# Revit family: NLRSen_57_AT_UN_PRxD_Solid_Air
name_source: partatom
category: Air Terminals
revit_build: Autodesk Revit 2017 (Build: 20190508_0315(x64)
units: mm (PartAtom-declared; Revit-internal decimal feet)

## family parameters
Always vertical = Yes
Cut with Voids When Loaded = No
OmniClass Number = 23.75.70.21.27.11
OmniClass Title = Diffusers, Registers, and Grilles
Part Type = Normal
Room Calculation Point = Yes
Round Connector Dimension = Use Diameter
Shared = No
Work Plane-Based = No

## types (5) — shared parameters
Description = Flanged perforated return grill, Type PRVD and PRDD
IfcDescription = Flanged perforated return grill, Type PRVD and PRDD
IfcExportAs = IfcAirterminal
IfcExportType = Diffuser
Lookup_Article_Codes = Grill_Article_Codes
Lookup_Article_Data = PRxD_Article_Data
Lookup_Article_Names = Grill_Article_Names
Lookup_Grill_Factors = Grill_Selection_Factors
Manufacturer = Solid Air Climate Solutions
Model = PRxD
NLRS_C_content_datum_uitgifte = 2019-09-17
NLRS_C_content_provider = Solid Air Climate Solutions
NLRS_C_content_versie = 2.03
NLRS_C_description = Flanged perforated return grill, Type PRVD and PRDD
SACS_AX_Prefix = 800
SACS_Plenum_Material = Sendzimir verzinkt
SACS_Revised_ by = J. Feeke
SACS_Revision_Date = 2019-09-17
SACS_Revision_Number = 2.03
Type Comments = Please make sure flow is set to m3/h!
URL = https://solid-air.nl
zero-valued in all types: Cost

## per-type parameters (varying)
| type | Assembly Code | Max Flow | Min Flow | SACS_Base_Index | SACS_Plenum_A | SACS_Plenum_B | SACS_Plenum_D1 | SACS_Plenum_D2 | SACS_Plenum_D2oval_H | SACS_Plenum_D2oval_W | SACS_Plenum_P | SACS_Plenum_Plow | SACS_Plenum_Poval | SACS_Plenum_T |
| 250 | 57.71 | 216 m³/h | 54 m³/h | 1 | 242 mm  [stored 0.793963 ft] | 249 mm  [stored 0.816929 ft] | 123 mm  [stored 0.403543 ft] | 123 mm  [stored 0.403543 ft] | 73 mm  [stored 0.239501 ft] | 164 mm  [stored 0.538058 ft] | 235 mm  [stored 0.770997 ft] | 220 mm  [stored 0.721785 ft] | 160 mm  [stored 0.524934 ft] | 70 mm  [stored 0.229659 ft] |
| 300 | 57 | 360 m³/h | 90 m³/h | 2 | 307 mm  [stored 1.00722 ft] | 313 mm  [stored 1.0269 ft] | 158 mm | 158 mm | 93 mm  [stored 0.305118 ft] | 208 mm | 270 mm  [stored 0.885827 ft] | 255 mm  [stored 0.836614 ft] | 180 mm  [stored 0.590551 ft] | 70 mm  [stored 0.229659 ft] |
| 400 | 57 | 540 m³/h | 144 m³/h | 3 | 382 mm  [stored 1.25328 ft] | 388 mm  [stored 1.27297 ft] | 198 mm  [stored 0.649606 ft] | 198 mm  [stored 0.649606 ft] | 117 mm  [stored 0.383858 ft] | 262 mm  [stored 0.85958 ft] | 315 mm  [stored 1.03346 ft] | 300 mm  [stored 0.984252 ft] | 210 mm  [stored 0.688976 ft] | 75 mm  [stored 0.246063 ft] |
| 500 | 57 | 720 m³/h | 216 m³/h | 4 | 477 mm  [stored 1.56496 ft] | 483 mm | 248 mm  [stored 0.813648 ft] | 198 mm  [stored 0.649606 ft] | 117 mm  [stored 0.383858 ft] | 262 mm  [stored 0.85958 ft] | 325 mm  [stored 1.06627 ft] | 310 mm  [stored 1.01706 ft] | 220 mm  [stored 0.721785 ft] | 85 mm  [stored 0.278871 ft] |
| 550 | 57 | 1080 m³/h | 288 m³/h | 5 | 551 mm  [stored 1.80774 ft] | 556 mm  [stored 1.82415 ft] | 313 mm  [stored 1.0269 ft] | 248 mm  [stored 0.813648 ft] | 147 mm  [stored 0.482283 ft] | 330 mm  [stored 1.08268 ft] | 395 mm  [stored 1.29593 ft] | 365 mm  [stored 1.19751 ft] | 270 mm  [stored 0.885827 ft] | 105 mm  [stored 0.344488 ft] |

note: [stored X ft] marks values corroborated as IEEE doubles in the binary element streams (Revit-internal decimal feet)

## geometry (parser evidence)
native form markers: Sweep x16
no freeform markers — native parametric forms only
